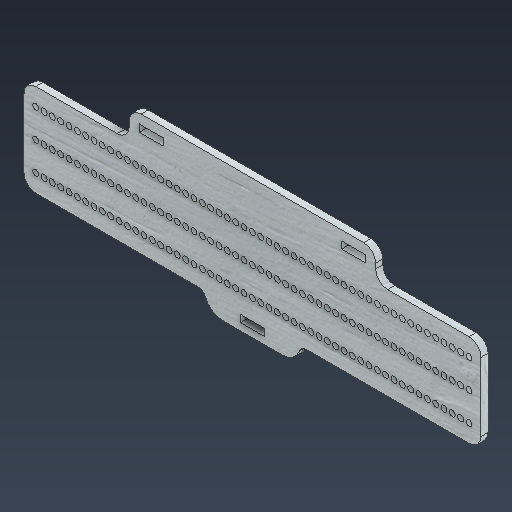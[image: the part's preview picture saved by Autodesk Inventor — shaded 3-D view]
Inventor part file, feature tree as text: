
AUTODESK INVENTOR PART (.ipt)
format: ipt  version: 2025.3 (Build 293356000, 356)  size: 509,952 bytes
history: native  units: mm
features: other x3, sketch x2, extrude x1
ambient origin geometry x8: Origin, YZ Plane, XZ Plane, XY Plane, X Axis, Y Axis, Z Axis, Center Point
bodies: Body1 (feature_tree)
feature tree (6):
  other  "實體1"
  extrude  "擠出1"  Depth=10.0mm
  sketch  "草圖3"
  sketch  "草圖1"
  other  "草圖 - 矩形陣列5"
  other  "草圖 - 矩形陣列15"
